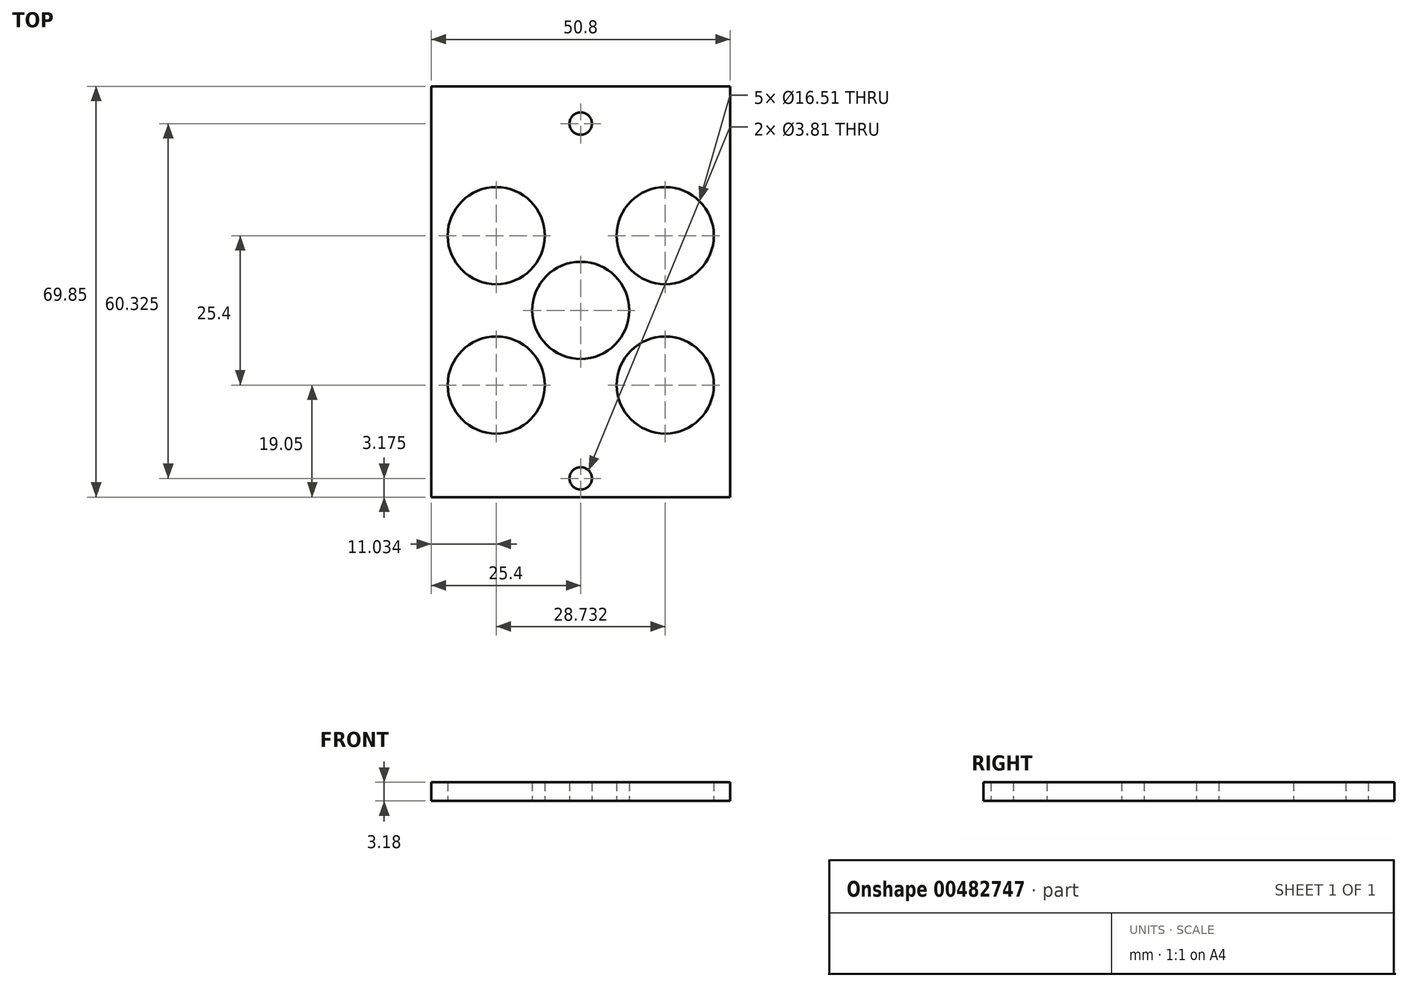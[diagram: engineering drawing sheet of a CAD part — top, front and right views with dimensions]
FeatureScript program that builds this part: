
annotation { "Feature Type Name" : "Feature", "Feature Type Description" : "" }
export const myFeature = defineFeature(function(context is Context, id is Id, definition is map)
    precondition{}
    {
        {
            var Q0;
            Q0=qCreatedBy(makeId("Top.planeOp"),FACE);
            var sketch = newSketch(context, id + "F0", { "sketchPlane" : qUnion([Q0])});
            skLineSegment(sketch, "E0", {"start": v(0, 39.41) * mm, "end": v(0, -31.75) * mm, "construction": true});
            skLineSegment(sketch, "E1.MirrorCS", {"start": v(25.4, 31.75) * mm, "end": v(25.4, -31.75) * mm, "construction": true});
            skLineSegment(sketch, "E2.0", {"start": v(14.37, 54.16) * mm, "end": v(14.37, -26.9) * mm, "construction": true});
            skPoint(sketch, "E3.orphan", {"position": v(25.4, -26.9) * mm});
            skPoint(sketch, "E4.orphan", {"position": v(-25.4, -26.9) * mm});
            skLineSegment(sketch, "E5.top", {"start": v(-25.4, -31.75) * mm, "end": v(25.4, -31.75) * mm});
            skCircle(sketch, "E6", {"center": v(0, 31.75) * mm, "radius": 1.9 * mm});
            skCircle(sketch, "E7", {"center": v(0, -28.58) * mm, "radius": 1.9 * mm});
            skLineSegment(sketch, "E8", {"start": v(-25.4, 25.4) * mm, "end": v(25.4, 25.4) * mm});
            skLineSegment(sketch, "E9", {"start": v(25.4, -25.4) * mm, "end": v(-25.4, -25.4) * mm});
            skLineSegment(sketch, "E10", {"start": v(-14.37, 38.1) * mm, "end": v(14.37, 38.1) * mm});
            skLineSegment(sketch, "E11.MirrorCS", {"start": v(-14.37, 54.16) * mm, "end": v(-14.37, -26.9) * mm, "construction": true});
            skCircle(sketch, "E12", {"center": v(-14.37, 12.7) * mm, "radius": 8.26 * mm});
            skCircle(sketch, "E13", {"center": v(14.37, 12.7) * mm, "radius": 8.26 * mm});
            skCircle(sketch, "E14", {"center": v(-14.37, -12.7) * mm, "radius": 8.26 * mm});
            skCircle(sketch, "E15", {"center": v(14.37, -12.7) * mm, "radius": 8.26 * mm});
            skCircle(sketch, "E16", {"center": v(0, 0) * mm, "radius": 8.26 * mm});
            skLineSegment(sketch, "E17.trimOffspring", {"start": v(-25.4, 31.75) * mm, "end": v(-25.4, -31.75) * mm, "construction": true});
            skLineSegment(sketch, "E18.trimOffspring", {"start": v(25.4, 31.75) * mm, "end": v(25.4, -31.75) * mm});
            skLineSegment(sketch, "E19.trimOffspring", {"start": v(-25.4, 31.75) * mm, "end": v(-25.4, -31.75) * mm});
            skLineSegment(sketch, "E20", {"start": v(-14.37, 38.1) * mm, "end": v(-25.4, 38.1) * mm});
            skLineSegment(sketch, "E21", {"start": v(-25.4, 38.1) * mm, "end": v(-25.4, 31.75) * mm});
            skLineSegment(sketch, "E22", {"start": v(14.37, 38.1) * mm, "end": v(25.4, 38.1) * mm});
            skLineSegment(sketch, "E23", {"start": v(25.4, 38.1) * mm, "end": v(25.4, 31.75) * mm});
            skSolve(sketch);
        }
        {
            var Q0;
            {var subQ0=sQuery(id+"F0.wireOp",EDGE,"E8");Q0=makeQuery(id+"F0.imprint","IMPRINT",FACE,{"disambiguationData":[TD([[makeQuery(id+"F0.imprint","IMPRINT",EDGE,{"derivedFrom":subQ0}),-1.0]])]});}
            var Q1;
            Q1=makeQuery(id+"F0.imprint","IMPRINT",FACE,{"disambiguationData":[TD([[makeQuery(id+"F0.imprint","IMPRINT",EDGE,{"derivedFrom":sQuery(id+"F0.wireOp",EDGE,"E6")}),-1.0]])]});
            var Q2;
            {var subQ1=sQuery(id+"F0.wireOp",EDGE,"E5.top");Q2=makeQuery(id+"F0.imprint","IMPRINT",FACE,{"disambiguationData":[TD([[makeQuery(id+"F0.imprint","IMPRINT",EDGE,{"derivedFrom":subQ1}),1.0]])]});}
            extrude(context, id + "F1", {"entities" : qUnion([Q0, Q1, Q2]), "depth" : 3.17 * mm});
        }
    });
